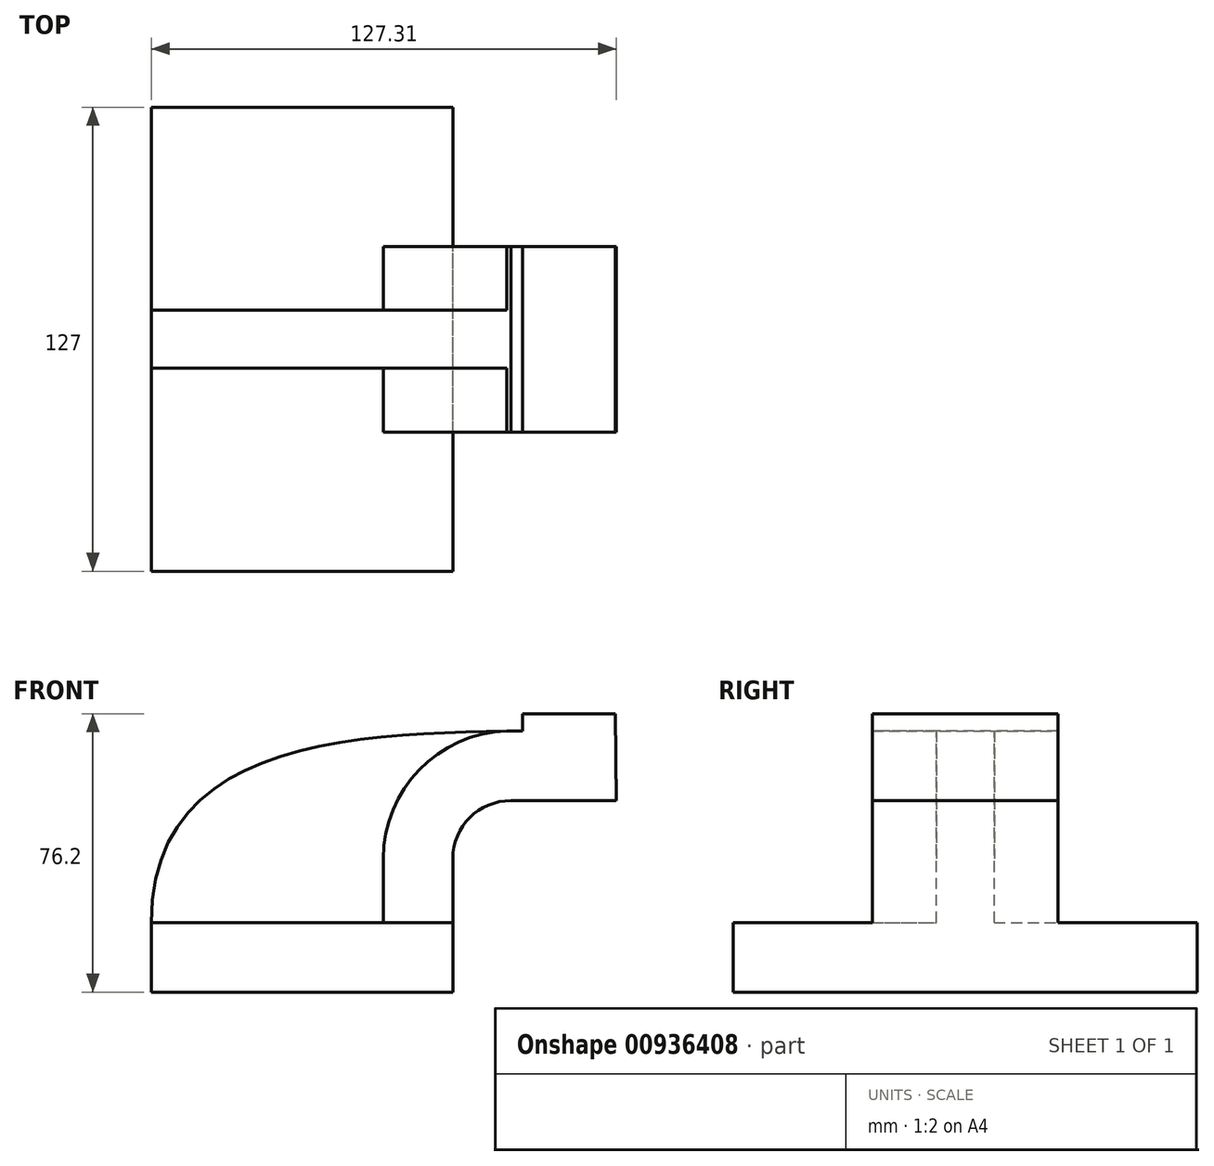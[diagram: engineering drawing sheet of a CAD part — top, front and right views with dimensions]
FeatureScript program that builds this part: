
annotation { "Feature Type Name" : "Feature", "Feature Type Description" : "" }
export const myFeature = defineFeature(function(context is Context, id is Id, definition is map)
    precondition{}
    {
        {
            var Q0;
            Q0=qCreatedBy(makeId("Front.planeOp"),FACE);
            var sketch = newSketch(context, id + "F0", { "sketchPlane" : qUnion([Q0])});
            skLineSegment(sketch, "E0.bottom", {"start": v(-41.28, -9.53) * mm, "end": v(41.28, -9.53) * mm});
            skLineSegment(sketch, "E0.top", {"start": v(-41.28, 9.53) * mm, "end": v(41.28, 9.53) * mm});
            skLineSegment(sketch, "E0.left", {"start": v(-41.28, -9.53) * mm, "end": v(-41.28, 9.53) * mm});
            skLineSegment(sketch, "E0.right", {"start": v(41.28, -9.53) * mm, "end": v(41.28, 9.53) * mm});
            skPoint(sketch, "E0.middle", {"position": v(0, 0) * mm});
            skLineSegment(sketch, "E1.bottom", {"start": v(60.32, 38.1) * mm, "end": v(111.12, 38.1) * mm});
            skLineSegment(sketch, "E1.top", {"start": v(60.32, 66.67) * mm, "end": v(111.12, 66.67) * mm});
            skLineSegment(sketch, "E1.left", {"start": v(60.32, 38.1) * mm, "end": v(60.32, 66.67) * mm});
            skLineSegment(sketch, "E1.right", {"start": v(111.12, 38.1) * mm, "end": v(111.12, 66.67) * mm});
            skPoint(sketch, "E1.middle", {"position": v(85.72, 52.39) * mm});
            skLineSegment(sketch, "E2", {"start": v(41.28, 9.53) * mm, "end": v(41.28, 27) * mm});
            skArc(sketch, "E3", {"start": v(41.28, 27) * mm, "mid": v(45.92, 38.23) * mm, "end": v(57.15, 42.88) * mm});
            skLineSegment(sketch, "E4", {"start": v(57.15, 42.88) * mm, "end": v(86.1, 42.88) * mm});
            skLineSegment(sketch, "E5.0", {"start": v(57.15, 61.93) * mm, "end": v(85.72, 61.93) * mm});
            skArc(sketch, "E5.1", {"start": v(22.23, 27) * mm, "mid": v(32.45, 51.7) * mm, "end": v(57.15, 61.93) * mm});
            skLineSegment(sketch, "E5.2", {"start": v(22.23, 9.53) * mm, "end": v(22.23, 27) * mm});
            skPoint(sketch, "E6.endSnap0", {"position": v(45.92, 38.23) * mm});
            skLineSegment(sketch, "E7", {"start": v(85.72, 66.67) * mm, "end": v(86.1, 38.1) * mm});
            skFitSpline(sketch, "E8", {"points": [v(-41.28, 9.53) * mm, v(57.15, 61.93) * mm], "startDerivative": vector(-0.35, 150.72) * mm, "endDerivative": vector(126.72, 1.99) * mm});
            skSolve(sketch);
        }
        {
            var Q0;
            Q0=makeQuery(id+"F0.imprint","IMPRINT",FACE,{"disambiguationData":[TD([[makeQuery(id+"F0.imprint","IMPRINT",EDGE,{"derivedFrom":sQuery(id+"F0.wireOp",EDGE,"E0.bottom")}),1.0]])]});
            extrude(context, id + "F1", {"entities" : qUnion([Q0]), "depth" : 127 * mm, "offsetDistance" : 25.4 * mm, "symmetric" : true});
        }
        {
            var Q0;
            {var subQ1=sQuery(id+"F0.wireOp",EDGE,"E2");Q0=makeQuery(id+"F0.imprint","IMPRINT",FACE,{"disambiguationData":[TD([[makeQuery(id+"F0.imprint","IMPRINT",EDGE,{"derivedFrom":subQ1}),1.0]])]});}
            var Q1;
            {var subQ1=sQuery(id+"F0.wireOp",EDGE,"E1.left");var subQ5=sQuery(id+"F0.wireOp",EDGE,"E1.top");var subQ6=makeQuery(id+"F0.imprint","INTERSECT",VERTEX,{"derivedFrom":[subQ5,subQ1]});Q1=makeQuery(id+"F0.imprint","IMPRINT",FACE,{"disambiguationData":[TD([[makeQuery(id+"F0.imprint","IMPRINT",EDGE,{"disambiguationData":[TD([[subQ6,-1.0]])],"derivedFrom":subQ5}),-1.0]])]});}
            extrude(context, id + "F2", {"entities" : qUnion([Q0, Q1]), "operationType" : NewBodyOperationType.ADD, "depth" : 50.8 * mm, "offsetDistance" : 25.4 * mm, "symmetric" : true});
        }
        {
            var Q0;
            {var subQ3=sQuery(id+"F0.wireOp",EDGE,"E5.2");Q0=makeQuery(id+"F0.imprint","IMPRINT",FACE,{"disambiguationData":[TD([[makeQuery(id+"F0.imprint","IMPRINT",EDGE,{"derivedFrom":subQ3}),1.0]])]});}
            extrude(context, id + "F3", {"entities" : qUnion([Q0]), "operationType" : NewBodyOperationType.ADD, "depth" : 15.88 * mm, "offsetDistance" : 25.4 * mm, "symmetric" : true});
        }
    });
